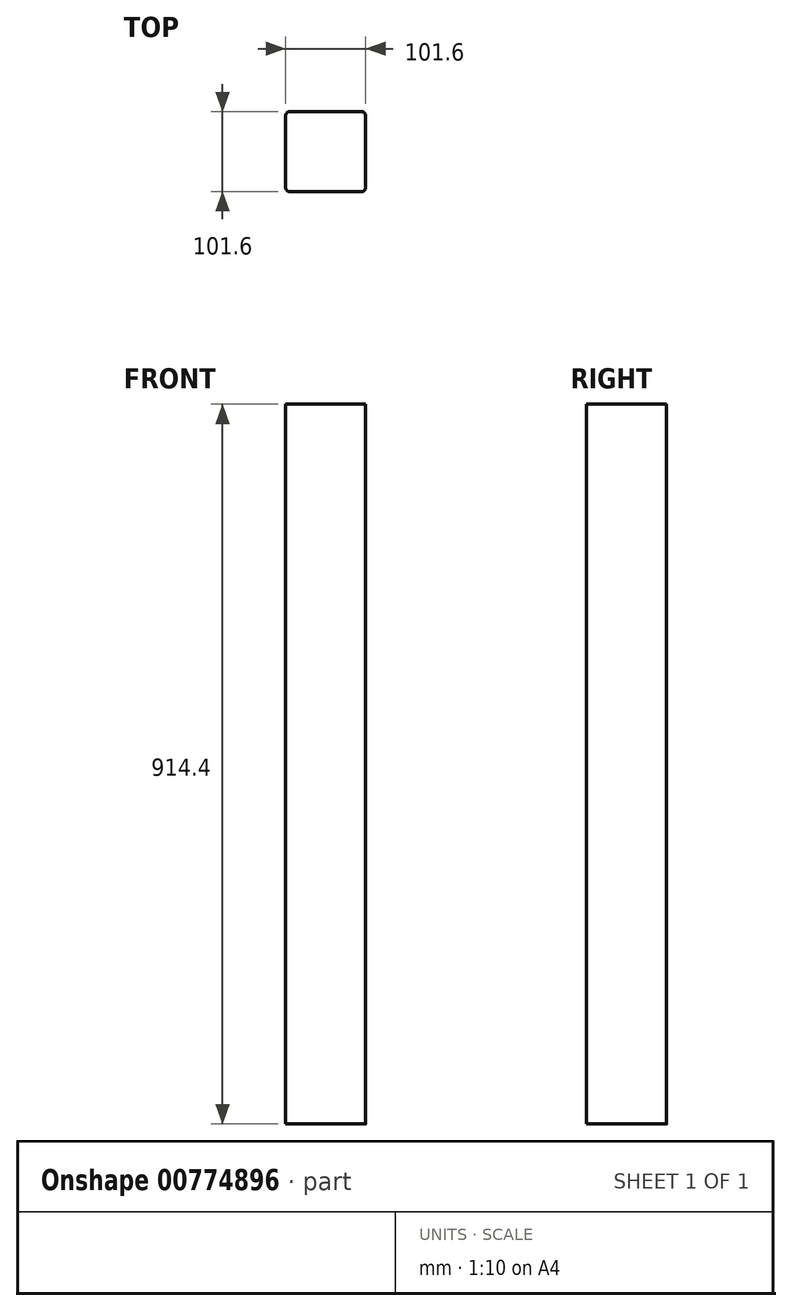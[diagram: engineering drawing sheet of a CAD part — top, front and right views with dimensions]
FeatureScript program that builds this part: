
annotation { "Feature Type Name" : "Feature", "Feature Type Description" : "" }
export const myFeature = defineFeature(function(context is Context, id is Id, definition is map)
    precondition{}
    {
        {
            var Q0;
            Q0=qCreatedBy(makeId("Top.planeOp"),FACE);
            var sketch = newSketch(context, id + "F0", { "sketchPlane" : qUnion([Q0])});
            skLineSegment(sketch, "E0.bottom", {"start": v(50.8, 50.8) * mm, "end": v(-50.8, 50.8) * mm});
            skLineSegment(sketch, "E0.top", {"start": v(50.8, -50.8) * mm, "end": v(-50.8, -50.8) * mm});
            skLineSegment(sketch, "E0.left", {"start": v(50.8, 50.8) * mm, "end": v(50.8, -50.8) * mm});
            skLineSegment(sketch, "E0.right", {"start": v(-50.8, 50.8) * mm, "end": v(-50.8, -50.8) * mm});
            skPoint(sketch, "E0.middle", {"position": v(0, 0) * mm});
            skSolve(sketch);
        }
        {
            var Q0;
            Q0 = qSketchRegion(id + "F0", true);
            extrude(context, id + "F1", {"entities" : qUnion([Q0]), "depth" : 914.4 * mm, "offsetDistance" : 25.4 * mm});
        }
        {
            var Q0;
            Q0=makeQuery(id+"F1.opExtrude","SWEPT_EDGE",EDGE,{"disambiguationData":[OSD([sQuery(id+"F0.wireOp",EDGE,"E0.bottom"),sQuery(id+"F0.wireOp",EDGE,"E0.left")])]});
            var Q1;
            Q1=makeQuery(id+"F1.opExtrude","SWEPT_EDGE",EDGE,{"disambiguationData":[OSD([sQuery(id+"F0.wireOp",EDGE,"E0.top"),sQuery(id+"F0.wireOp",EDGE,"E0.left")])]});
            var Q2;
            Q2=makeQuery(id+"F1.opExtrude","SWEPT_EDGE",EDGE,{"disambiguationData":[OSD([sQuery(id+"F0.wireOp",EDGE,"E0.bottom"),sQuery(id+"F0.wireOp",EDGE,"E0.right")])]});
            var Q3;
            Q3=makeQuery(id+"F1.opExtrude","SWEPT_EDGE",EDGE,{"disambiguationData":[OSD([sQuery(id+"F0.wireOp",EDGE,"E0.top"),sQuery(id+"F0.wireOp",EDGE,"E0.right")])]});
            fillet(context, id + "F2", {"entities" : qUnion([Q0, Q1, Q2, Q3]), "radius" : 5.08 * mm, "tangentPropagation" : true, "allowEdgeOverflow" : false});
        }
    });
